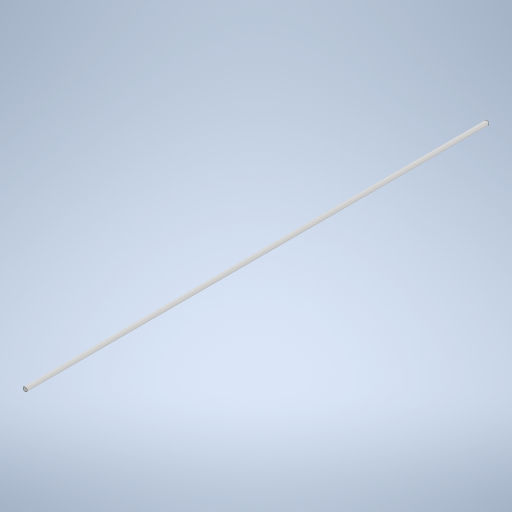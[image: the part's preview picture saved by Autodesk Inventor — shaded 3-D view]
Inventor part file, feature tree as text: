
AUTODESK INVENTOR PART (.ipt)
format: ipt  version: 2023 (Build 270158000, 158)  size: 235,008 bytes
history: native  units: mm
features: other x1, extrude x1, sketch x1
ambient origin geometry x8: Origin, YZ Plane, XZ Plane, XY Plane, X Axis, Y Axis, Z Axis, Center Point
bodies: Solid1 (feature_tree)
feature tree (3):
  other  "Welle"
  extrude  "Extrusion1"  Depth=440.0mm TaperAngle=0.0deg
  sketch  "Sketch1"  dims[d0=4.0mm d1=440.0mm d2=0.0mm]
